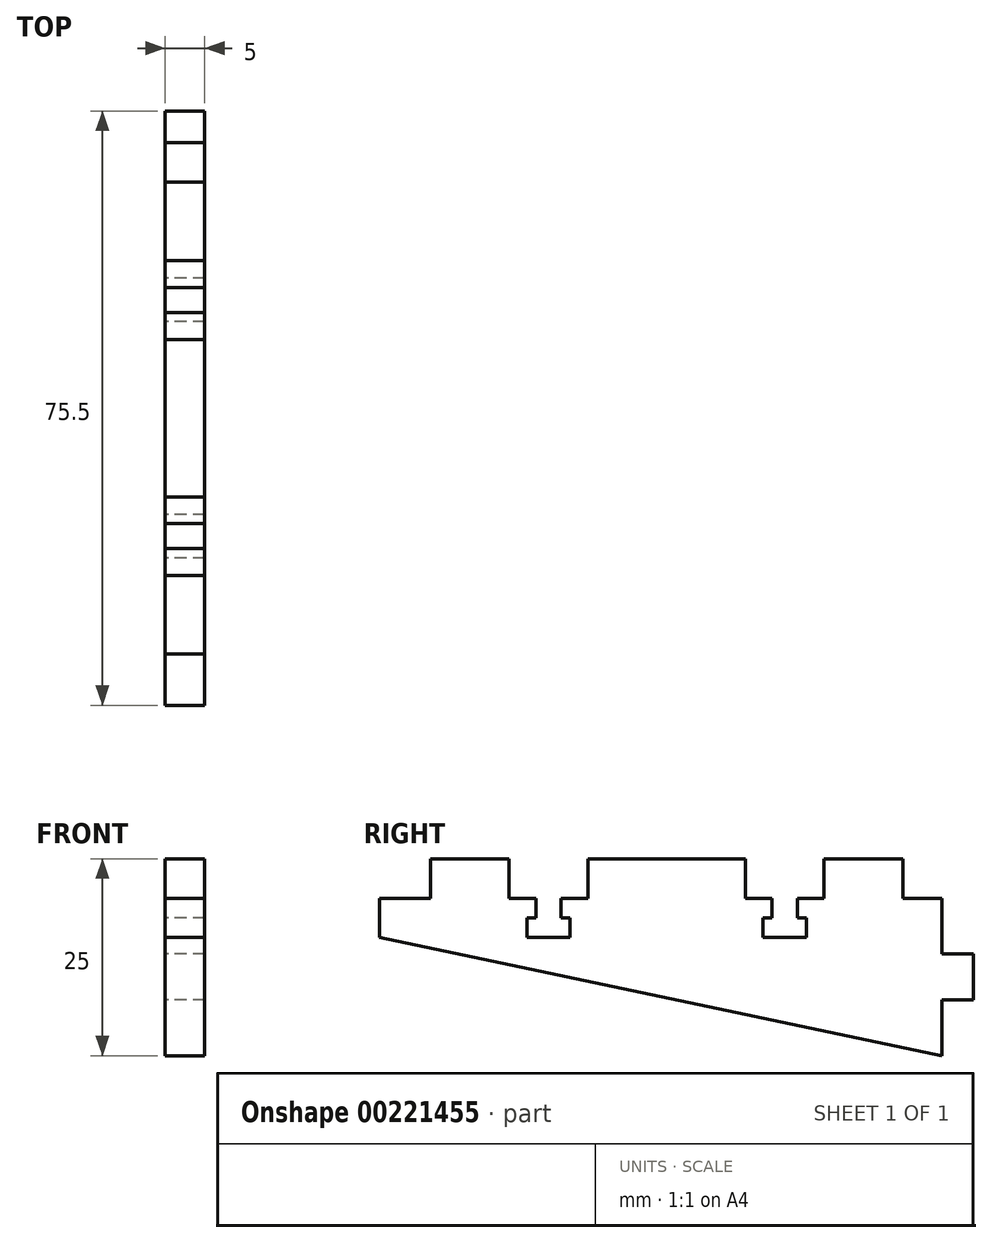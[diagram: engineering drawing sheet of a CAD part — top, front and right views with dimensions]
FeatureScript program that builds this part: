
annotation { "Feature Type Name" : "Feature", "Feature Type Description" : "" }
export const myFeature = defineFeature(function(context is Context, id is Id, definition is map)
    precondition{}
    {
        {
            assignVariable(context, id + "F0", {"name" : "thickness", "anyValue" : 5 * mm});
        }
        {
            var Q0;
            Q0=qCreatedBy(makeId("Right.planeOp"),FACE);
            var sketch = newSketch(context, id + "F1", { "sketchPlane" : qUnion([Q0])});
            skLineSegment(sketch, "E0", {"start": v(0, 0) * mm, "end": v(0, 7.1) * mm});
            skLineSegment(sketch, "E1", {"start": v(0, 20) * mm, "end": v(-5, 20) * mm});
            skLineSegment(sketch, "E2", {"start": v(-5, 20) * mm, "end": v(-5, 25) * mm});
            skLineSegment(sketch, "E3", {"start": v(-5, 25) * mm, "end": v(-15, 25) * mm});
            skLineSegment(sketch, "E4", {"start": v(-15, 25) * mm, "end": v(-15, 20) * mm});
            skLineSegment(sketch, "E5", {"start": v(-25, 20) * mm, "end": v(-25, 25) * mm});
            skLineSegment(sketch, "E6", {"start": v(-25, 25) * mm, "end": v(-45, 25) * mm});
            skLineSegment(sketch, "E7", {"start": v(-45, 25) * mm, "end": v(-45, 20) * mm});
            skLineSegment(sketch, "E8", {"start": v(-55, 20) * mm, "end": v(-55, 25) * mm});
            skLineSegment(sketch, "E9", {"start": v(-55, 25) * mm, "end": v(-65, 25) * mm});
            skLineSegment(sketch, "E10", {"start": v(-65, 25) * mm, "end": v(-65, 20) * mm});
            skLineSegment(sketch, "E11.trimOffspring", {"start": v(-65, 20) * mm, "end": v(-71.5, 20) * mm});
            skLineSegment(sketch, "E12.trimOffspring", {"start": v(-45, 20) * mm, "end": v(-48.4, 20) * mm});
            skLineSegment(sketch, "E13.trimOffspring", {"start": v(-15, 20) * mm, "end": v(-18.4, 20) * mm});
            skLineSegment(sketch, "E14", {"start": v(-20, 20) * mm, "end": v(-20, 4.2) * mm, "construction": true});
            skLineSegment(sketch, "E15", {"start": v(-35, 25) * mm, "end": v(-35, 7.34) * mm, "construction": true});
            skLineSegment(sketch, "E16", {"start": v(-21.6, 20) * mm, "end": v(-21.6, 17.5) * mm});
            skLineSegment(sketch, "E17", {"start": v(-21.6, 17.5) * mm, "end": v(-22.75, 17.5) * mm});
            skLineSegment(sketch, "E18", {"start": v(-22.75, 17.5) * mm, "end": v(-22.75, 15) * mm});
            skLineSegment(sketch, "E19", {"start": v(-22.75, 15) * mm, "end": v(-20, 15) * mm});
            skLineSegment(sketch, "E20.MirrorCS", {"start": v(-17.25, 15) * mm, "end": v(-20, 15) * mm});
            skLineSegment(sketch, "E21.MirrorCS", {"start": v(-17.25, 17.5) * mm, "end": v(-17.25, 15) * mm});
            skLineSegment(sketch, "E22.MirrorCS", {"start": v(-18.4, 17.5) * mm, "end": v(-17.25, 17.5) * mm});
            skLineSegment(sketch, "E23.MirrorCS", {"start": v(-18.4, 20) * mm, "end": v(-18.4, 17.5) * mm});
            skLineSegment(sketch, "E24.MirrorCS", {"start": v(-48.4, 20) * mm, "end": v(-48.4, 17.5) * mm});
            skLineSegment(sketch, "E25.MirrorCS", {"start": v(-48.4, 17.5) * mm, "end": v(-47.25, 17.5) * mm});
            skLineSegment(sketch, "E26.MirrorCS", {"start": v(-47.25, 17.5) * mm, "end": v(-47.25, 15) * mm});
            skLineSegment(sketch, "E27.MirrorCS", {"start": v(-47.25, 15) * mm, "end": v(-50, 15) * mm});
            skLineSegment(sketch, "E28.MirrorCS", {"start": v(-52.75, 15) * mm, "end": v(-50, 15) * mm});
            skLineSegment(sketch, "E29.MirrorCS", {"start": v(-52.75, 17.5) * mm, "end": v(-52.75, 15) * mm});
            skLineSegment(sketch, "E30.MirrorCS", {"start": v(-51.6, 20) * mm, "end": v(-51.6, 17.5) * mm});
            skLineSegment(sketch, "E31.MirrorCS", {"start": v(-51.6, 17.5) * mm, "end": v(-52.75, 17.5) * mm});
            skLineSegment(sketch, "E32.trimOffspring", {"start": v(-51.6, 20) * mm, "end": v(-55, 20) * mm});
            skLineSegment(sketch, "E33.trimOffspring", {"start": v(-21.6, 20) * mm, "end": v(-25, 20) * mm});
            skLineSegment(sketch, "E34", {"start": v(-71.5, 20) * mm, "end": v(-71.5, 15) * mm});
            skLineSegment(sketch, "E35", {"start": v(-71.5, 15) * mm, "end": v(0, 0) * mm});
            skLineSegment(sketch, "E36", {"start": v(0, 12.9) * mm, "end": v(4, 12.9) * mm});
            skLineSegment(sketch, "E37", {"start": v(4, 12.9) * mm, "end": v(4, 7.1) * mm});
            skLineSegment(sketch, "E38", {"start": v(4, 7.1) * mm, "end": v(0, 7.1) * mm});
            skPoint(sketch, "E39", {"position": v(4, 10) * mm});
            skPoint(sketch, "E40", {"position": v(0, 10) * mm});
            skLineSegment(sketch, "E41.trimOffspring", {"start": v(0, 12.9) * mm, "end": v(0, 20) * mm});
            skSolve(sketch);
        }
        {
            var Q0;
            Q0 = qSketchRegion(id + "F1", true);
            extrude(context, id + "F2", {"entities" : qUnion([Q0]), "depth" : getVariable(context, 'thickness')});
        }
    });
